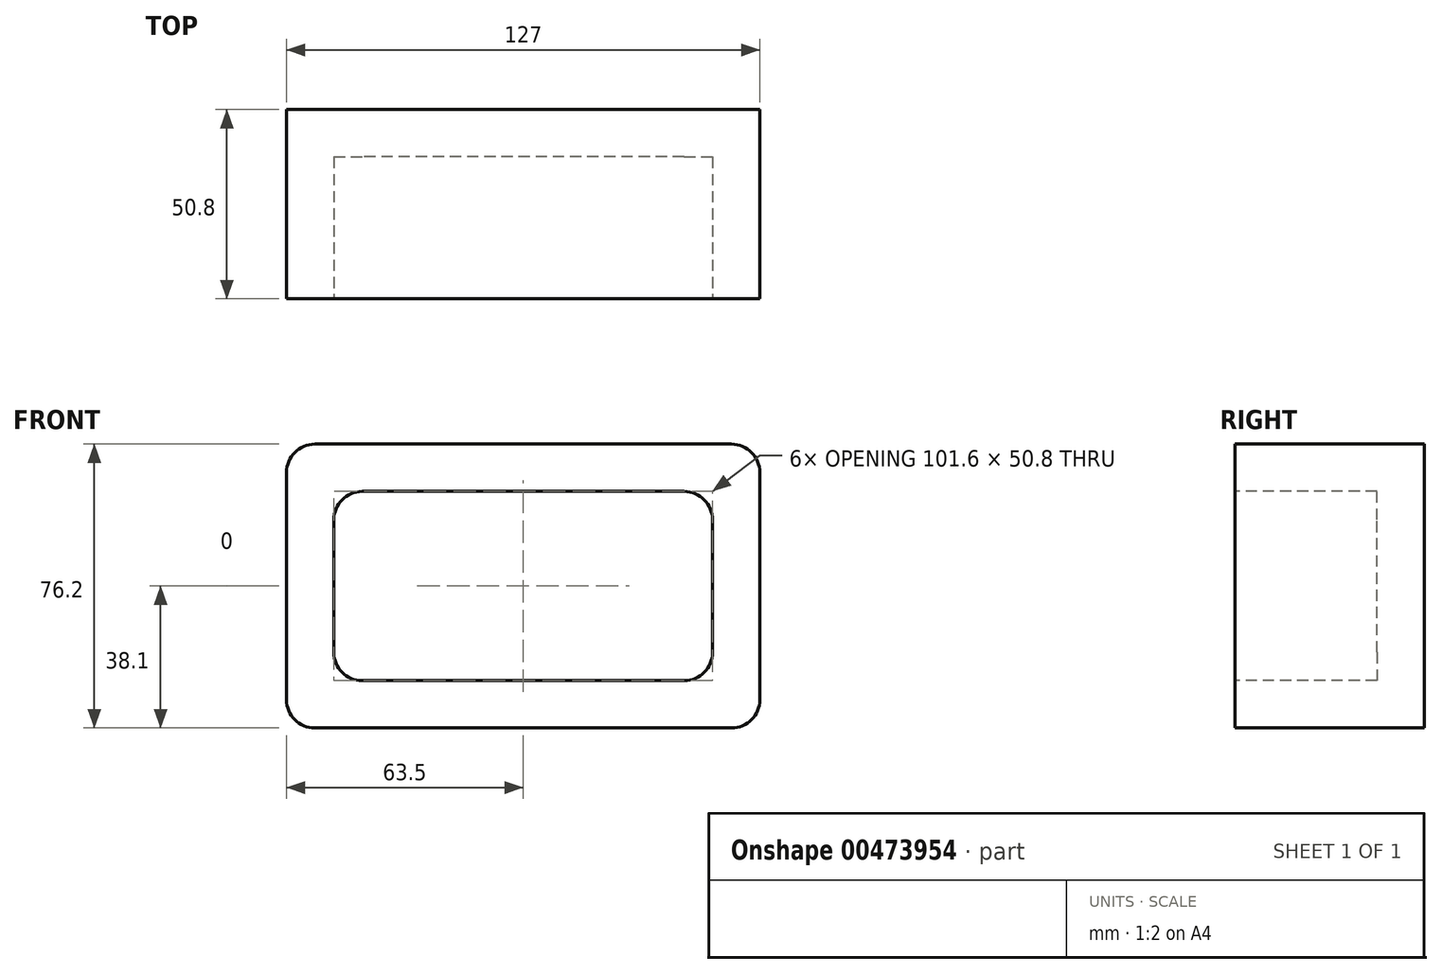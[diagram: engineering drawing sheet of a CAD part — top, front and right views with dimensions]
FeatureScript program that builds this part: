
annotation { "Feature Type Name" : "Feature", "Feature Type Description" : "" }
export const myFeature = defineFeature(function(context is Context, id is Id, definition is map)
    precondition{}
    {
        {
            var Q0;
            Q0=qCreatedBy(makeId("Front.planeOp"),FACE);
            var sketch = newSketch(context, id + "F0", { "sketchPlane" : qUnion([Q0])});
            skLineSegment(sketch, "E0.bottom", {"start": v(63.5, -38.1) * mm, "end": v(-63.5, -38.1) * mm});
            skLineSegment(sketch, "E0.top", {"start": v(63.5, 38.1) * mm, "end": v(-63.5, 38.1) * mm});
            skLineSegment(sketch, "E0.left", {"start": v(63.5, -38.1) * mm, "end": v(63.5, 38.1) * mm});
            skLineSegment(sketch, "E0.right", {"start": v(-63.5, -38.1) * mm, "end": v(-63.5, 38.1) * mm});
            skPoint(sketch, "E0.middle", {"position": v(0, 0) * mm});
            skSolve(sketch);
        }
        {
            var Q0;
            Q0 = qSketchRegion(id + "F0", true);
            extrude(context, id + "F1", {"entities" : qUnion([Q0]), "oppositeDirection" : true, "depth" : 50.8 * mm, "offsetDistance" : 25.4 * mm});
        }
        {
            var Q0;
            Q0=makeQuery(id+"F1.opExtrude","CAP_FACE",FACE,{"disambiguationData":[OSD([sQuery(id+"F0.wireOp",EDGE,"E0.bottom"),sQuery(id+"F0.wireOp",EDGE,"E0.top"),sQuery(id+"F0.wireOp",EDGE,"E0.left"),sQuery(id+"F0.wireOp",EDGE,"E0.right")])],"isStart":true});
            var sketch = newSketch(context, id + "F2", { "sketchPlane" : qUnion([Q0])});
            skLineSegment(sketch, "E1.bottom", {"start": v(50.8, -25.4) * mm, "end": v(-50.8, -25.4) * mm});
            skLineSegment(sketch, "E1.top", {"start": v(50.8, 25.4) * mm, "end": v(-50.8, 25.4) * mm});
            skLineSegment(sketch, "E1.left", {"start": v(50.8, -25.4) * mm, "end": v(50.8, 25.4) * mm});
            skLineSegment(sketch, "E1.right", {"start": v(-50.8, -25.4) * mm, "end": v(-50.8, 25.4) * mm});
            skPoint(sketch, "E1.middle", {"position": v(0, 0) * mm});
            skSolve(sketch);
        }
        {
            var Q0;
            Q0 = qSketchRegion(id + "F2", true);
            extrude(context, id + "F3", {"entities" : qUnion([Q0]), "operationType" : NewBodyOperationType.REMOVE, "oppositeDirection" : true, "depth" : 38.1 * mm, "offsetDistance" : 25.4 * mm});
        }
        {
            var Q0;
            Q0=makeQuery(id+"F3.boolean.opBoolean","COPY",EDGE,{"derivedFrom":makeQuery(id+"F3.opExtrude","SWEPT_EDGE",EDGE,{"disambiguationData":[OSD([sQuery(id+"F2.wireOp",EDGE,"E1.top"),sQuery(id+"F2.wireOp",EDGE,"E1.right")])]})});
            var Q1;
            Q1=makeQuery(id+"F3.boolean.opBoolean","COPY",EDGE,{"derivedFrom":makeQuery(id+"F3.opExtrude","SWEPT_EDGE",EDGE,{"disambiguationData":[OSD([sQuery(id+"F2.wireOp",EDGE,"E1.top"),sQuery(id+"F2.wireOp",EDGE,"E1.left")])]})});
            var Q2;
            Q2=makeQuery(id+"F3.boolean.opBoolean","COPY",EDGE,{"derivedFrom":makeQuery(id+"F3.opExtrude","SWEPT_EDGE",EDGE,{"disambiguationData":[OSD([sQuery(id+"F2.wireOp",EDGE,"E1.bottom"),sQuery(id+"F2.wireOp",EDGE,"E1.left")])]})});
            var Q3;
            Q3=makeQuery(id+"F3.boolean.opBoolean","COPY",EDGE,{"derivedFrom":makeQuery(id+"F3.opExtrude","SWEPT_EDGE",EDGE,{"disambiguationData":[OSD([sQuery(id+"F2.wireOp",EDGE,"E1.bottom"),sQuery(id+"F2.wireOp",EDGE,"E1.right")])]})});
            var Q4;
            Q4=makeQuery(id+"F1.opExtrude","SWEPT_EDGE",EDGE,{"disambiguationData":[OSD([sQuery(id+"F0.wireOp",EDGE,"E0.bottom"),sQuery(id+"F0.wireOp",EDGE,"E0.right")])]});
            var Q5;
            Q5=makeQuery(id+"F1.opExtrude","SWEPT_EDGE",EDGE,{"disambiguationData":[OSD([sQuery(id+"F0.wireOp",EDGE,"E0.bottom"),sQuery(id+"F0.wireOp",EDGE,"E0.left")])]});
            var Q6;
            Q6=makeQuery(id+"F1.opExtrude","SWEPT_EDGE",EDGE,{"disambiguationData":[OSD([sQuery(id+"F0.wireOp",EDGE,"E0.top"),sQuery(id+"F0.wireOp",EDGE,"E0.left")])]});
            var Q7;
            Q7=makeQuery(id+"F1.opExtrude","SWEPT_EDGE",EDGE,{"disambiguationData":[OSD([sQuery(id+"F0.wireOp",EDGE,"E0.top"),sQuery(id+"F0.wireOp",EDGE,"E0.right")])]});
            fillet(context, id + "F4", {"entities" : qUnion([Q0, Q1, Q2, Q3, Q4, Q5, Q6, Q7]), "radius" : 7.62 * mm, "tangentPropagation" : true, "allowEdgeOverflow" : false});
        }
    });
